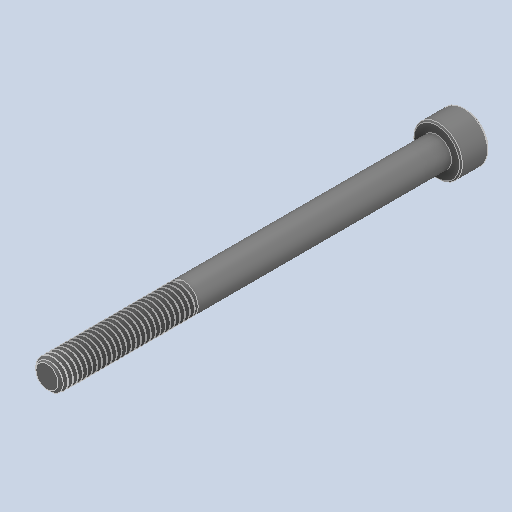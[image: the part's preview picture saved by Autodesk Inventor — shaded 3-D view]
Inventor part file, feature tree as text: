
AUTODESK INVENTOR PART (.ipt)
format: ipt  version: 2024.2 (Build 282272000, 272)  size: 666,624 bytes
history: native  units: in
note: dims shown in document units (in); Inventor stores cm internally (conversion verified against a paired STEP export)
features: chamfer x1
ambient origin geometry x8: Origin, YZ Plane, XZ Plane, XY Plane, X Axis, Y Axis, Z Axis, Center Point
bodies: Solid1 (feature_tree)
feature tree (1):
  chamfer  "Chamfer2"  [1 undecoded]
note: 1 required parameter value undecoded (feature->parameter linkage not recoverable at this tier; creation-order binding heuristic only, values carry confidence <= 0.55)
